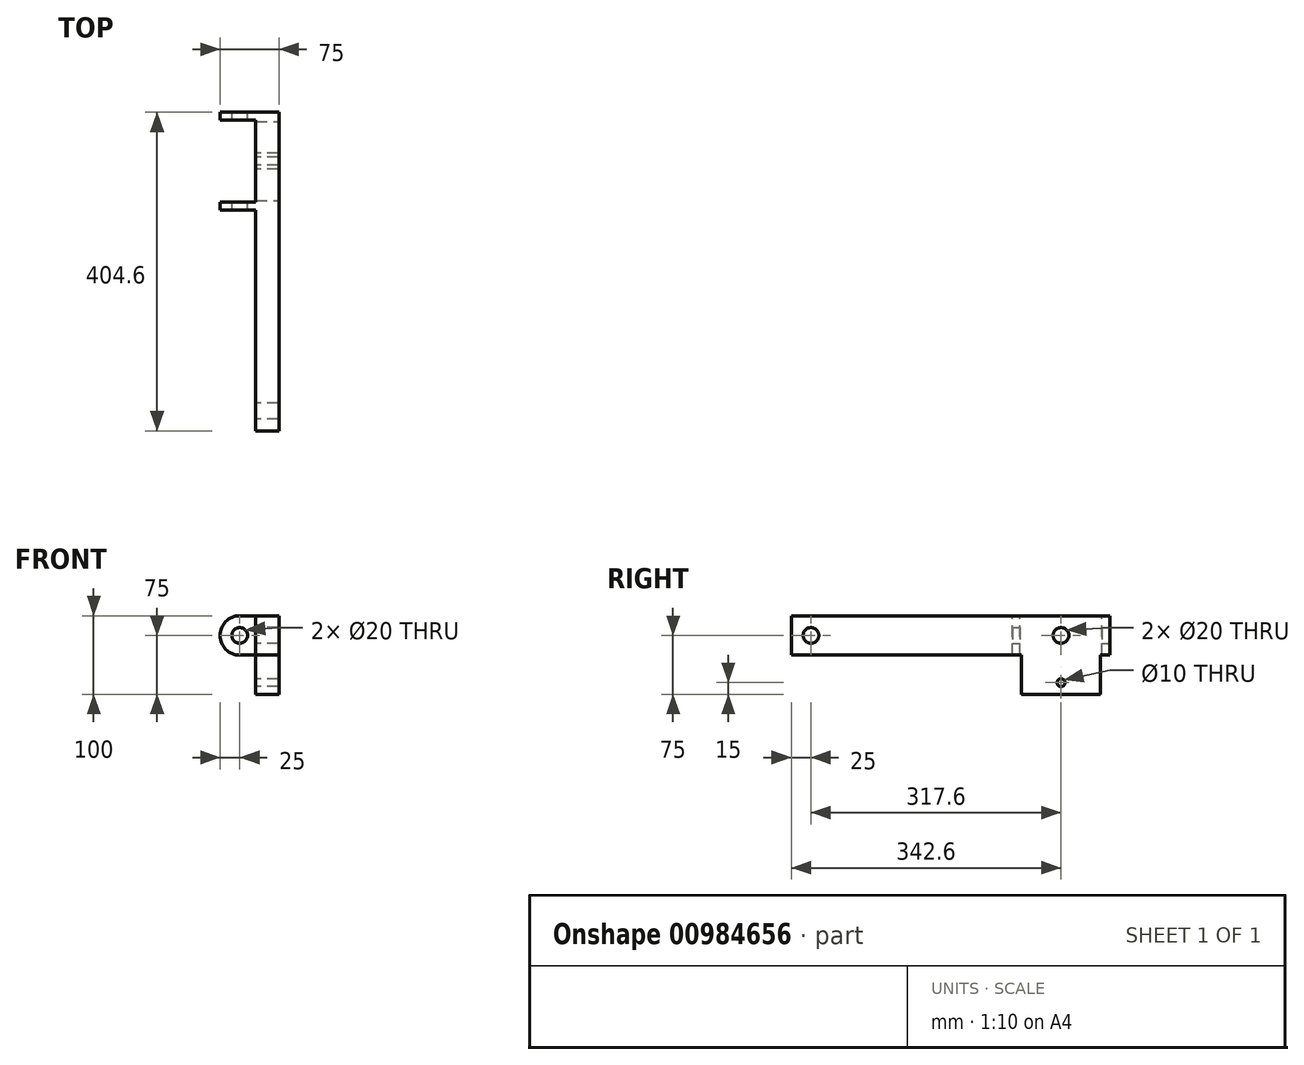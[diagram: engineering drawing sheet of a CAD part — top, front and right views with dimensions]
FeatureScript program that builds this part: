
annotation { "Feature Type Name" : "Feature", "Feature Type Description" : "" }
export const myFeature = defineFeature(function(context is Context, id is Id, definition is map)
    precondition{}
    {
        {
            var Q0;
            Q0=qCreatedBy(makeId("Front.planeOp"),FACE);
            var sketch = newSketch(context, id + "F0", { "sketchPlane" : qUnion([Q0])});
            skLineSegment(sketch, "E0.bottom", {"start": v(0, 0) * mm, "end": v(30, 0) * mm});
            skLineSegment(sketch, "E0.top", {"start": v(0, 50) * mm, "end": v(30, 50) * mm});
            skLineSegment(sketch, "E0.left", {"start": v(0, 0) * mm, "end": v(0, 50) * mm});
            skLineSegment(sketch, "E0.right", {"start": v(30, 0) * mm, "end": v(30, 50) * mm});
            skSolve(sketch);
        }
        {
            var Q0;
            Q0=makeQuery(id+"F0.imprint","IMPRINT",FACE,{"disambiguationData":[TD([[makeQuery(id+"F0.imprint","IMPRINT",EDGE,{"derivedFrom":sQuery(id+"F0.wireOp",EDGE,"E0.bottom")}),1.0]])]});
            extrude(context, id + "F1", {"entities" : qUnion([Q0]), "depth" : 400 * mm, "offsetDistance" : 25 * mm});
        }
        {
            var Q0;
            Q0=qCreatedBy(makeId("Right.planeOp"),FACE);
            var sketch = newSketch(context, id + "F2", { "sketchPlane" : qUnion([Q0])});
            skPoint(sketch, "E1", {"position": v(-375, 25) * mm});
            skPoint(sketch, "E2", {"position": v(-57.4, 25) * mm});
            skSolve(sketch);
        }
        {
            var Q0;
            Q0=sQuery(id+"F2.wireOp",VERTEX,"E1");
            var Q1;
            Q1=sQuery(id+"F2.wireOp",VERTEX,"E2");
            var Q2;
            Q2=makeQuery(id+"F1.opExtrude","SWEPT_BODY",BODY,{"disambiguationData":[OSD([sQuery(id+"F0.wireOp",EDGE,"E0.bottom"),sQuery(id+"F0.wireOp",EDGE,"E0.top"),sQuery(id+"F0.wireOp",EDGE,"E0.left"),sQuery(id+"F0.wireOp",EDGE,"E0.right")])]});
            hole(context, id + "F3", {"style" : HoleStyle.SIMPLE, "endStyle" : HoleEndStyle.THROUGH, "oppositeDirection" : true, "holeDiameter" : 20 * mm, "majorDiameter" : 5 * mm, "isTappedThrough" : true, "tappedDepth" : 12 * mm, "tapClearance" : 3, "locations" : qUnion([Q0, Q1]), "scope" : qUnion([Q2])});
        }
        {
            var Q0;
            Q0 = qSketchRegion(id + "F0", true);
            extrude(context, id + "F4", {"entities" : qUnion([Q0]), "operationType" : NewBodyOperationType.ADD, "oppositeDirection" : true, "depth" : 4.6 * mm, "offsetDistance" : 25 * mm});
        }
        {
            var Q0;
            Q0=qCreatedBy(makeId("Right.planeOp"),FACE);
            var sketch = newSketch(context, id + "F5", { "sketchPlane" : qUnion([Q0])});
            skLineSegment(sketch, "E3.bottom", {"start": v(-5.4, 0) * mm, "end": v(4.6, 0) * mm});
            skLineSegment(sketch, "E3.top", {"start": v(-5.4, 50) * mm, "end": v(4.6, 50) * mm});
            skLineSegment(sketch, "E3.left", {"start": v(-5.4, 0) * mm, "end": v(-5.4, 50) * mm});
            skLineSegment(sketch, "E3.right", {"start": v(4.6, 0) * mm, "end": v(4.6, 50) * mm});
            skLineSegment(sketch, "E4.bottom", {"start": v(-109.4, 0) * mm, "end": v(-119.4, 0) * mm});
            skLineSegment(sketch, "E4.top", {"start": v(-109.4, 50) * mm, "end": v(-119.4, 50) * mm});
            skLineSegment(sketch, "E4.left", {"start": v(-109.4, 0) * mm, "end": v(-109.4, 50) * mm});
            skLineSegment(sketch, "E4.right", {"start": v(-119.4, 0) * mm, "end": v(-119.4, 50) * mm});
            skPoint(sketch, "E5", {"position": v(-57.4, 25) * mm});
            skSolve(sketch);
        }
        {
            var Q0;
            Q0 = qSketchRegion(id + "F5", true);
            extrude(context, id + "F6", {"entities" : qUnion([Q0]), "operationType" : NewBodyOperationType.ADD, "oppositeDirection" : true, "depth" : 20 * mm, "offsetDistance" : 25 * mm});
        }
        {
            var Q0;
            Q0=makeQuery(id+"F6.opExtrude","CAP_FACE",FACE,{"disambiguationData":[OSD([sQuery(id+"F5.wireOp",EDGE,"E3.bottom"),sQuery(id+"F5.wireOp",EDGE,"E3.top"),sQuery(id+"F5.wireOp",EDGE,"E3.left"),sQuery(id+"F5.wireOp",EDGE,"E3.right")])],"isStart":false});
            var sketch = newSketch(context, id + "F7", { "sketchPlane" : qUnion([Q0])});
            skLineSegment(sketch, "E6.bottom", {"start": v(5.4, 0) * mm, "end": v(-4.6, 0) * mm});
            skLineSegment(sketch, "E6.top", {"start": v(5.4, 25) * mm, "end": v(-4.6, 25) * mm});
            skLineSegment(sketch, "E6.left", {"start": v(5.4, 0) * mm, "end": v(5.4, 25) * mm});
            skLineSegment(sketch, "E6.right", {"start": v(-4.6, 0) * mm, "end": v(-4.6, 25) * mm});
            skLineSegment(sketch, "E7", {"start": v(-16.26, 25) * mm, "end": v(17.08, 25) * mm, "construction": true});
            skSolve(sketch);
        }
        {
            var Q0;
            Q0 = qSketchRegion(id + "F7", true);
            var Q1;
            Q1=sQuery(id+"F7.wireOp",EDGE,"E7");
            revolve(context, id + "F8", {"operationType" : NewBodyOperationType.ADD, "surfaceOperationType" : NewSurfaceOperationType.NEW, "entities" : qUnion([Q0]), "axis" : qUnion([Q1]), "revolveType" : RevolveType.FULL});
        }
        {
            var Q0;
            Q0=makeQuery(id+"F6.opExtrude","CAP_FACE",FACE,{"disambiguationData":[OSD([sQuery(id+"F5.wireOp",EDGE,"E4.bottom"),sQuery(id+"F5.wireOp",EDGE,"E4.top"),sQuery(id+"F5.wireOp",EDGE,"E4.left"),sQuery(id+"F5.wireOp",EDGE,"E4.right")])],"isStart":false});
            var sketch = newSketch(context, id + "F9", { "sketchPlane" : qUnion([Q0])});
            skLineSegment(sketch, "E8.bottom", {"start": v(119.4, 0) * mm, "end": v(109.4, 0) * mm});
            skLineSegment(sketch, "E8.top", {"start": v(119.4, 25) * mm, "end": v(109.4, 25) * mm});
            skLineSegment(sketch, "E8.left", {"start": v(119.4, 0) * mm, "end": v(119.4, 25) * mm});
            skLineSegment(sketch, "E8.right", {"start": v(109.4, 0) * mm, "end": v(109.4, 25) * mm});
            skLineSegment(sketch, "E9", {"start": v(100.49, 25) * mm, "end": v(127.67, 25) * mm, "construction": true});
            skSolve(sketch);
        }
        {
            var Q0;
            Q0=makeQuery(id+"F9.imprint","IMPRINT",FACE,{"disambiguationData":[TD([[makeQuery(id+"F9.imprint","IMPRINT",EDGE,{"derivedFrom":sQuery(id+"F9.wireOp",EDGE,"E8.bottom")}),1.0]])]});
            var Q1;
            Q1=sQuery(id+"F9.wireOp",EDGE,"E9");
            revolve(context, id + "F10", {"operationType" : NewBodyOperationType.ADD, "surfaceOperationType" : NewSurfaceOperationType.NEW, "entities" : qUnion([Q0]), "axis" : qUnion([Q1]), "revolveType" : RevolveType.FULL});
        }
        {
            var Q0;
            Q0=makeQuery(id+"F8.boolean.opBoolean","MERGE",FACE,{"derivedFrom":[makeQuery(id+"F6.boolean.opBoolean","MERGE",FACE,{"derivedFrom":[makeQuery(id+"F4.opExtrude","CAP_FACE",FACE,{"disambiguationData":[OSD([sQuery(id+"F0.wireOp",EDGE,"E0.bottom"),sQuery(id+"F0.wireOp",EDGE,"E0.top"),sQuery(id+"F0.wireOp",EDGE,"E0.left"),sQuery(id+"F0.wireOp",EDGE,"E0.right")])],"isStart":false}),makeQuery(id+"F6.opExtrude","SWEPT_FACE",FACE,{"disambiguationData":[OSD([sQuery(id+"F5.wireOp",EDGE,"E3.right")])]})]}),makeQuery(id+"F8.opRevolve","SWEPT_FACE",FACE,{"disambiguationData":[OSD([sQuery(id+"F7.wireOp",EDGE,"E6.right")])]})]});
            var sketch = newSketch(context, id + "F11", { "sketchPlane" : qUnion([Q0])});
            skPoint(sketch, "E10", {"position": v(20, 25) * mm});
            skSolve(sketch);
        }
        {
            var Q0;
            Q0=sQuery(id+"F11.wireOp",VERTEX,"E10");
            var Q1;
            Q1=makeQuery(id+"F1.opExtrude","SWEPT_BODY",BODY,{"disambiguationData":[OSD([sQuery(id+"F0.wireOp",EDGE,"E0.bottom"),sQuery(id+"F0.wireOp",EDGE,"E0.top"),sQuery(id+"F0.wireOp",EDGE,"E0.left"),sQuery(id+"F0.wireOp",EDGE,"E0.right")])]});
            hole(context, id + "F12", {"style" : HoleStyle.SIMPLE, "endStyle" : HoleEndStyle.THROUGH, "holeDiameter" : 20 * mm, "majorDiameter" : 5 * mm, "isTappedThrough" : true, "tappedDepth" : 12 * mm, "tapClearance" : 3, "locations" : qUnion([Q0]), "scope" : qUnion([Q1])});
        }
        {
            var Q0;
            {var subQ0=sQuery(id+"F0.wireOp",EDGE,"E0.bottom");Q0=makeQuery(id+"F6.boolean.opBoolean","MERGE",FACE,{"derivedFrom":[makeQuery(id+"F4.boolean.opBoolean","MERGE",FACE,{"derivedFrom":[makeQuery(id+"F1.opExtrude","SWEPT_FACE",FACE,{"disambiguationData":[OSD([subQ0])]}),makeQuery(id+"F4.opExtrude","SWEPT_FACE",FACE,{"disambiguationData":[OSD([subQ0])]})]}),makeQuery(id+"F6.opExtrude","SWEPT_FACE",FACE,{"disambiguationData":[OSD([sQuery(id+"F5.wireOp",EDGE,"E3.bottom")])]}),makeQuery(id+"F6.opExtrude","SWEPT_FACE",FACE,{"disambiguationData":[OSD([sQuery(id+"F5.wireOp",EDGE,"E4.bottom")])]})]});}
            var sketch = newSketch(context, id + "F13", { "sketchPlane" : qUnion([Q0])});
            skLineSegment(sketch, "E11.bottom", {"start": v(0, 107.4) * mm, "end": v(30, 107.4) * mm});
            skLineSegment(sketch, "E11.top", {"start": v(0, 7.4) * mm, "end": v(30, 7.4) * mm});
            skLineSegment(sketch, "E11.left", {"start": v(0, 107.4) * mm, "end": v(0, 7.4) * mm});
            skLineSegment(sketch, "E11.right", {"start": v(30, 107.4) * mm, "end": v(30, 7.4) * mm});
            skSolve(sketch);
        }
        {
            var Q0;
            Q0 = qSketchRegion(id + "F13", true);
            extrude(context, id + "F14", {"entities" : qUnion([Q0]), "operationType" : NewBodyOperationType.ADD, "depth" : 50 * mm, "offsetDistance" : 25 * mm});
        }
        {
            var Q0;
            {var subQ2=sQuery(id+"F0.wireOp",EDGE,"E0.left");Q0=makeQuery(id+"F14.boolean.opBoolean","MERGE",FACE,{"derivedFrom":[makeQuery(id+"F6.boolean.opBoolean","SPLIT",FACE,{"disambiguationData":[TD([makeQuery(id+"F3.hole-1.boolean.opBoolean","COPY",FACE,{"derivedFrom":makeQuery(id+"F3.hole-1.opRevolve","SWEPT_FACE",FACE,{"disambiguationData":[OSD([sQuery(id+"F3.hole-1.sketch.wireOp",EDGE,"core_line_2")])]})})])],"derivedFrom":makeQuery(id+"F4.boolean.opBoolean","MERGE",FACE,{"derivedFrom":[makeQuery(id+"F1.opExtrude","SWEPT_FACE",FACE,{"disambiguationData":[OSD([subQ2])]}),makeQuery(id+"F4.opExtrude","SWEPT_FACE",FACE,{"disambiguationData":[OSD([subQ2])]})]})}),makeQuery(id+"F14.opExtrude","SWEPT_FACE",FACE,{"disambiguationData":[OSD([sQuery(id+"F13.wireOp",EDGE,"E11.left")])]})]});}
            var sketch = newSketch(context, id + "F15", { "sketchPlane" : qUnion([Q0])});
            skPoint(sketch, "E12", {"position": v(57.4, -35) * mm});
            skSolve(sketch);
        }
        {
            var Q0;
            Q0=sQuery(id+"F15.wireOp",VERTEX,"E12");
            var Q1;
            Q1=makeQuery(id+"F1.opExtrude","SWEPT_BODY",BODY,{"disambiguationData":[OSD([sQuery(id+"F0.wireOp",EDGE,"E0.bottom"),sQuery(id+"F0.wireOp",EDGE,"E0.top"),sQuery(id+"F0.wireOp",EDGE,"E0.left"),sQuery(id+"F0.wireOp",EDGE,"E0.right")])]});
            hole(context, id + "F16", {"style" : HoleStyle.SIMPLE, "endStyle" : HoleEndStyle.THROUGH, "holeDiameter" : 10 * mm, "majorDiameter" : 5 * mm, "isTappedThrough" : true, "tappedDepth" : 12 * mm, "tapClearance" : 3, "locations" : qUnion([Q0]), "scope" : qUnion([Q1])});
        }
    });
